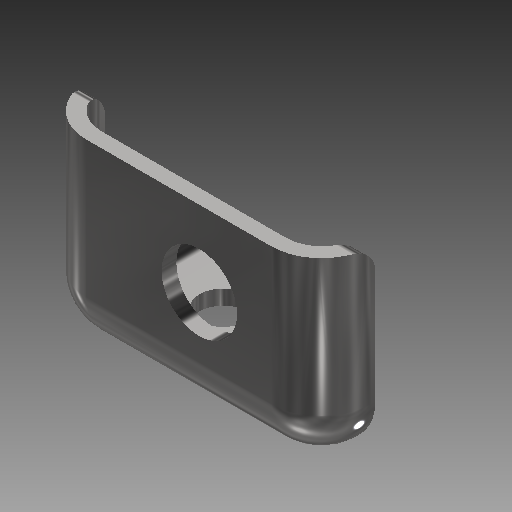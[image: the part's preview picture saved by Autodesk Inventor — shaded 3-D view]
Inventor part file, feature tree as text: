
AUTODESK INVENTOR PART (.ipt)
format: ipt  version: 2019 (Build 230136000, 136)  size: 233,472 bytes
history: native  units: mm
features: sketch x5, extrude x3, projected_geometry x3, fillet x2, hole x2, shell x1
ambient origin geometry x8: Origin, YZ Plane, XZ Plane, XY Plane, X Axis, Y Axis, Z Axis, Center Point
bodies: Solid1 (feature_tree)
feature tree (16):
  extrude  "Extrusion1"  Depth=48.283mm
  fillet  "Fillet1"  Radius=24.1415mm
  shell  "Shell1"  Thickness=15.787mm
  extrude  "Extrusion2"  Depth=8.5mm
  extrude  "Extrusion3"  Depth=17.0mm
  fillet  "Fillet2"  Radius=24.0mm
  hole  "Hole1"  [1 undecoded]
  hole  "Hole2"  [1 undecoded]
  sketch  "Sketch1"  dims[d0=31.574mm d1=48.283mm d2=24.1415mm d3=15.787mm]
  sketch  "Sketch2"  dims[d4=26.136mm d5=0.0mm d6=8.5mm]
  sketch  "Sketch3"  dims[d7=2.5mm d8=17.0mm d9=24.0mm]
  sketch  "Sketch4"  dims[d10=26.136mm d11=0.0mm d12=5.0mm]
  projected_geometry  "Projected Loop1"
  projected_geometry  "Projected Loop2"
  sketch  "Sketch5"  dims[d13=20.0mm d14=26.136mm d15=0.0mm d16=4.0mm d17=27.606mm d18=18.698mm d19=12.8mm d20=6.0mm d21=4.0mm d22=2.0mm d23=90.0deg d24=8.0mm d25=20.594885mm d26=15.663mm d27=15.98mm d28=8.0mm d29=6.0mm d30=4.0mm d31=2.0mm d32=90.0deg d33=8.0mm d34=20.594885mm]
  projected_geometry  "Projected Loop3"
note: 2 required parameter values undecoded (feature->parameter linkage not recoverable at this tier; creation-order binding heuristic only, values carry confidence <= 0.55)
